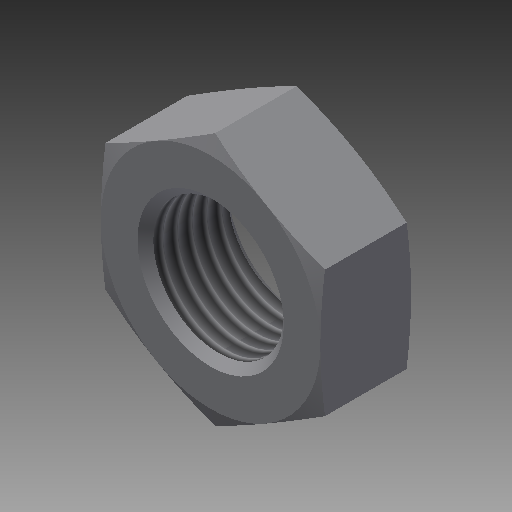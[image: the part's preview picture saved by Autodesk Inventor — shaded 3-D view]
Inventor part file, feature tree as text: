
AUTODESK INVENTOR PART (.ipt)
format: ipt  version: 2018.3 (Build 223284000, 284)  size: 186,368 bytes
history: native  units: in
note: dims shown in document units (in); Inventor stores cm internally (conversion verified against a paired STEP export)
features: other x70, sketch x3, revolve x2, extrude x1, thread x1
ambient origin geometry x8: Origin, YZ Plane, XZ Plane, XY Plane, X Axis, Y Axis, Z Axis, Center Point
bodies: Solid1 (feature_tree)
feature tree (77):
  sketch  "Sketch_8"  dims[d0=360.0deg d1=0.31in d2=0.0in]
  sketch  "Sketch_10"  dims[d3=360.0deg d4=0.2559in d5=0.0in]
  revolve  "Revolution1"  [1 undecoded]
  extrude  "Extrusion1"  Depth=0.2559in TaperAngle=0.0deg
  revolve  "Revolution2"  [1 undecoded]
  thread  "Thread1"  [1 undecoded]
  other  "NUT_XY"
  other  "NUT_YZ"
  other  "NUT_ZX"
  other  "NUT_X"
  other  "NUT_Y"
  other  "NUT_Z"
  other  "NUT_Center"
  other  "a1_XY"
  other  "a1_YZ"
  other  "a1_ZX"
  other  "a1_X"
  other  "a1_Y"
  other  "a1_Z"
  other  "a1_Center"
  other  "a2_XY"
  other  "a2_YZ"
  other  "a2_ZX"
  other  "a2_X"
  other  "a2_Y"
  other  "a2_Z"
  other  "a2_Center"
  other  "b1_XY"
  other  "b1_YZ"
  other  "b1_ZX"
  other  "b1_X"
  other  "b1_Y"
  other  "b1_Z"
  other  "b1_Center"
  other  "b2_XY"
  other  "b2_YZ"
  other  "b2_ZX"
  other  "b2_X"
  other  "b2_Y"
  other  "b2_Z"
  other  "b2_Center"
  other  "e_XY"
  other  "e_YZ"
  other  "e_ZX"
  other  "e_X"
  other  "e_Y"
  other  "e_Z"
  other  "e_Center"
  other  "ol1_XY"
  other  "ol1_YZ"
  other  "ol1_ZX"
  other  "ol1_X"
  other  "ol1_Y"
  other  "ol1_Z"
  other  "ol1_Center"
  other  "ol2_XY"
  other  "ol2_YZ"
  other  "ol2_ZX"
  other  "ol2_X"
  other  "ol2_Y"
  other  "ol2_Z"
  other  "ol2_Center"
  other  "th1_XY"
  other  "th1_YZ"
  other  "th1_ZX"
  other  "th1_X"
  other  "th1_Y"
  other  "th1_Z"
  other  "th1_Center"
  other  "th2_XY"
  other  "th2_YZ"
  other  "th2_ZX"
  other  "th2_X"
  other  "th2_Y"
  other  "th2_Z"
  other  "th2_Center"
  sketch  "Sketch_11"  dims[d6=0.0in d7=0.0in d8=0.0in]
note: 3 required parameter values undecoded (feature->parameter linkage not recoverable at this tier; creation-order binding heuristic only, values carry confidence <= 0.55)